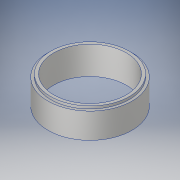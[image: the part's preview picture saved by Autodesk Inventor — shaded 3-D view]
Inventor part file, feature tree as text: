
AUTODESK INVENTOR PART (.ipt)
format: ipt  version: 2017 SP1 (Build 210196100, 196)  size: 146,944 bytes
history: native  units: in
note: dims shown in document units (in); Inventor stores cm internally (conversion verified against a paired STEP export)
features: revolve x1, sketch x1
ambient origin geometry x8: Origin, YZ Plane, XZ Plane, XY Plane, X Axis, Y Axis, Z Axis, Center Point
bodies: Body1 (feature_tree)
feature tree (2):
  revolve  "Revolution2"  [1 undecoded]
  sketch  "Sketch1"  dims[d0=0.5in d1=1.13in d3=15.0deg d4=0.25in d9=1.5in d11=0.5in d13=3.75in d14=0.25in d15=1.0in d16=0.25in d17=0.5in d18=0.234in d19=0.234in d20=0.5in d22=4.25in d23=2.5in d25=1.0in d26=0.25in d27=5.25in d28=0.125in d29=4.0in d30=0.25in d31=0.1718in d32=1.75in d33=0.125in d34=0.801in d35=0.375in d38=90.0deg]
note: 1 required parameter value undecoded (feature->parameter linkage not recoverable at this tier; creation-order binding heuristic only, values carry confidence <= 0.55)
